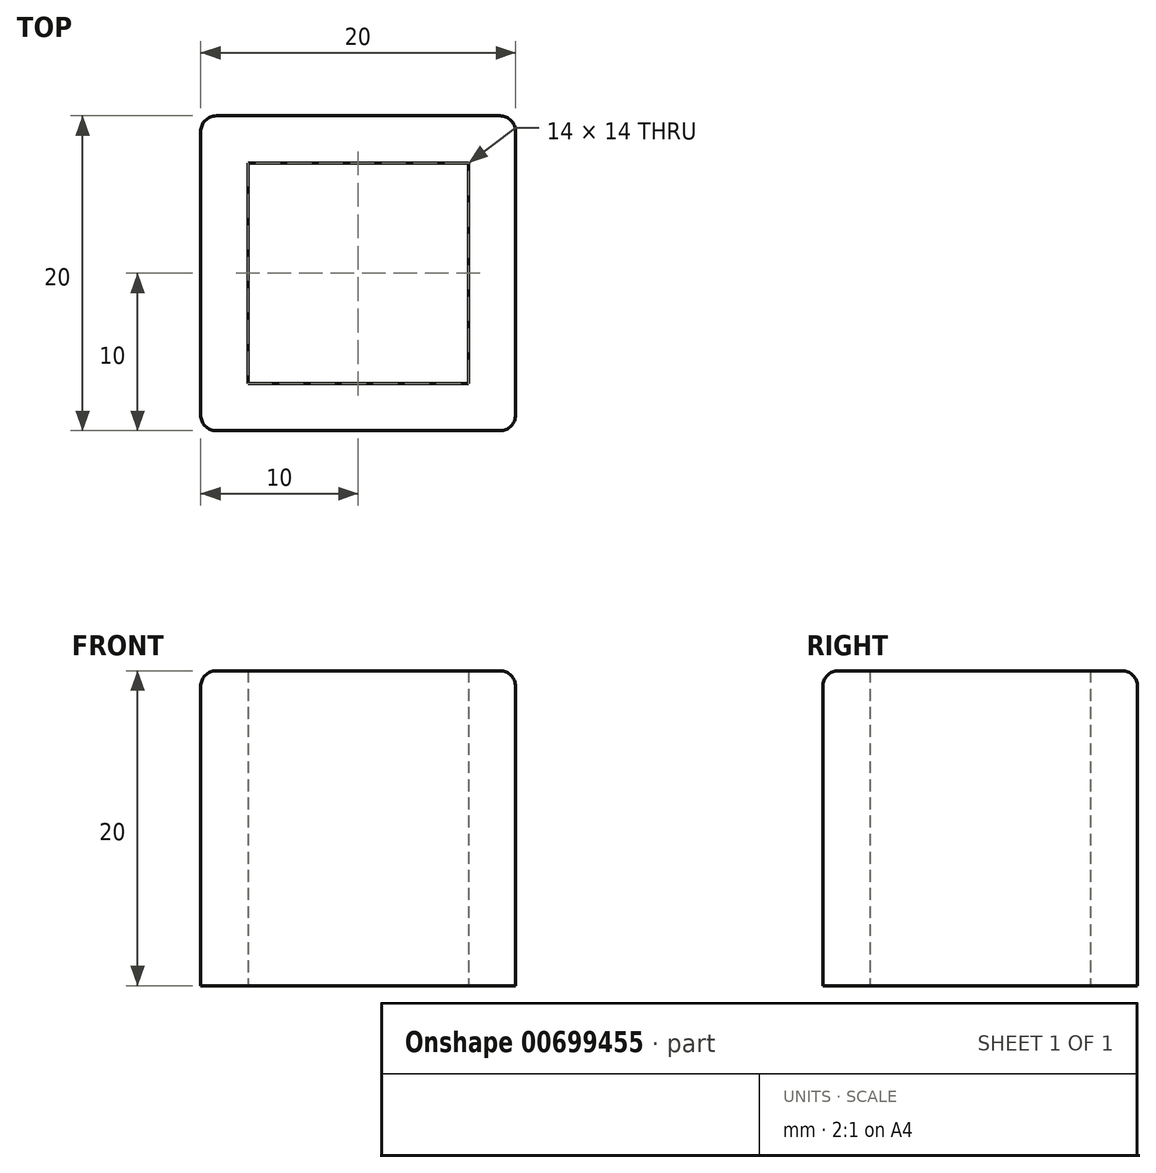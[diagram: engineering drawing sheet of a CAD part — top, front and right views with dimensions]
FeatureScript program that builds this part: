
annotation { "Feature Type Name" : "Feature", "Feature Type Description" : "" }
export const myFeature = defineFeature(function(context is Context, id is Id, definition is map)
    precondition{}
    {
        {
            var Q0;
            Q0=qCreatedBy(makeId("Top.planeOp"),FACE);
            var sketch = newSketch(context, id + "F0", { "sketchPlane" : qUnion([Q0])});
            skLineSegment(sketch, "E0.bottom", {"start": v(10, 10) * mm, "end": v(-10, 10) * mm});
            skLineSegment(sketch, "E0.top", {"start": v(10, -10) * mm, "end": v(-10, -10) * mm});
            skLineSegment(sketch, "E0.left", {"start": v(10, 10) * mm, "end": v(10, -10) * mm});
            skLineSegment(sketch, "E0.right", {"start": v(-10, 10) * mm, "end": v(-10, -10) * mm});
            skPoint(sketch, "E0.middle", {"position": v(0, 0) * mm});
            skLineSegment(sketch, "E1.0", {"start": v(7, -7) * mm, "end": v(-7, -7) * mm});
            skLineSegment(sketch, "E1.1", {"start": v(7, 7) * mm, "end": v(7, -7) * mm});
            skLineSegment(sketch, "E1.2", {"start": v(7, 7) * mm, "end": v(-7, 7) * mm});
            skLineSegment(sketch, "E1.3", {"start": v(-7, 7) * mm, "end": v(-7, -7) * mm});
            skSolve(sketch);
        }
        {
            var Q0;
            Q0=qSketchRegion(id+"F0",true);
            extrude(context, id + "F1", {"entities" : qUnion([Q0]), "depth" : 20 * mm, "offsetDistance" : 25 * mm});
        }
        {
            var Q0;
            Q0=makeQuery(id+"F1.opExtrude","CAP_EDGE",EDGE,{"disambiguationData":[OSD([sQuery(id+"F0.wireOp",EDGE,"E0.right")])],"isStart":false});
            var Q1;
            Q1=makeQuery(id+"F1.opExtrude","CAP_EDGE",EDGE,{"disambiguationData":[OSD([sQuery(id+"F0.wireOp",EDGE,"E0.bottom")])],"isStart":false});
            var Q2;
            Q2=makeQuery(id+"F1.opExtrude","CAP_EDGE",EDGE,{"disambiguationData":[OSD([sQuery(id+"F0.wireOp",EDGE,"E0.left")])],"isStart":false});
            var Q3;
            Q3=makeQuery(id+"F1.opExtrude","SWEPT_EDGE",EDGE,{"disambiguationData":[OSD([sQuery(id+"F0.wireOp",EDGE,"E0.bottom"),sQuery(id+"F0.wireOp",EDGE,"E0.left")])]});
            var Q4;
            Q4=makeQuery(id+"F1.opExtrude","SWEPT_EDGE",EDGE,{"disambiguationData":[OSD([sQuery(id+"F0.wireOp",EDGE,"E0.top"),sQuery(id+"F0.wireOp",EDGE,"E0.left")])]});
            var Q5;
            Q5=makeQuery(id+"F1.opExtrude","CAP_EDGE",EDGE,{"disambiguationData":[OSD([sQuery(id+"F0.wireOp",EDGE,"E0.top")])],"isStart":false});
            var Q6;
            Q6=makeQuery(id+"F1.opExtrude","SWEPT_EDGE",EDGE,{"disambiguationData":[OSD([sQuery(id+"F0.wireOp",EDGE,"E0.top"),sQuery(id+"F0.wireOp",EDGE,"E0.right")])]});
            var Q7;
            Q7=makeQuery(id+"F1.opExtrude","SWEPT_EDGE",EDGE,{"disambiguationData":[OSD([sQuery(id+"F0.wireOp",EDGE,"E0.bottom"),sQuery(id+"F0.wireOp",EDGE,"E0.right")])]});
            fillet(context, id + "F2", {"entities" : qUnion([Q0, Q1, Q2, Q3, Q4, Q5, Q6, Q7]), "radius" : 1 * mm, "tangentPropagation" : true, "allowEdgeOverflow" : false});
        }
    });
